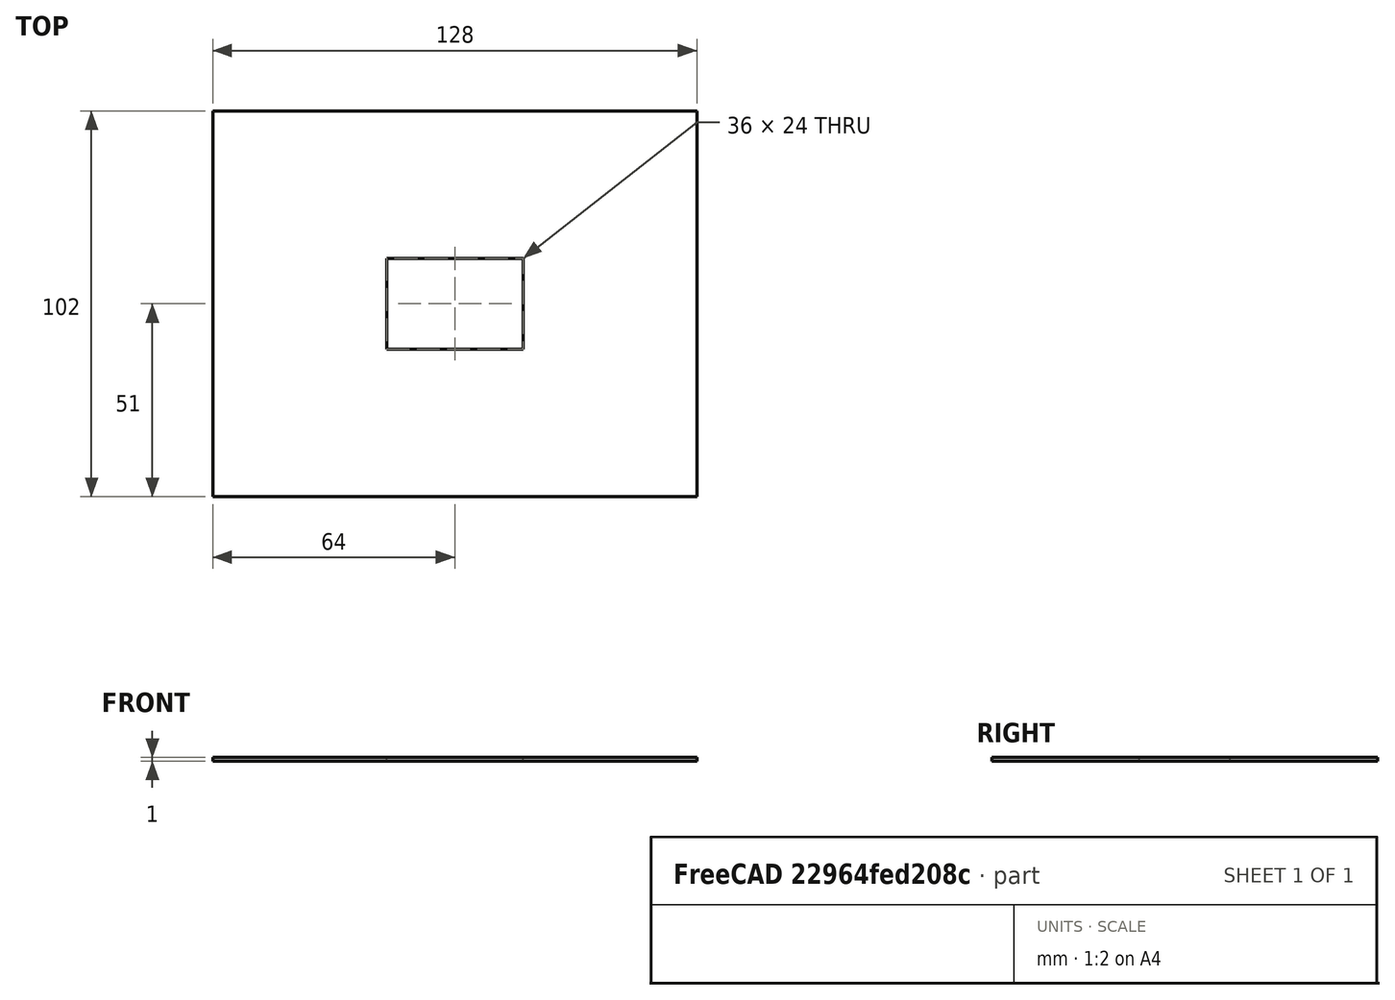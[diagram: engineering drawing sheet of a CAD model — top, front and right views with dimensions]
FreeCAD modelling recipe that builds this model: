
FCSTD DOCUMENT  (FreeCAD 0.18.4R)
Label: 35mm-mask
License: All rights reserved
LicenseURL: http://en.wikipedia.org/wiki/All_rights_reserved
objects: Sketcher::SketchObject×1, PartDesign::Pad×1, PartDesign::Body×1
note: 4 computed .brp shape members not serialized (recipe doc carries the construction recipe); baked Part::Feature solids carry a one-line shape summary decoded from their .brp

FEATURE [Sketcher::SketchObject] Sketch
  MapMode = 5
  Support = -> [XY_Plane]
  sketch-geometry (8):
    g0: LineSegment StartX=64 StartY=-51 StartZ=0 EndX=-64 EndY=-51 EndZ=0
    g1: LineSegment StartX=-64 StartY=-51 StartZ=0 EndX=-64 EndY=51 EndZ=0
    g2: LineSegment StartX=-64 StartY=51 StartZ=0 EndX=64 EndY=51 EndZ=0
    g3: LineSegment StartX=64 StartY=51 StartZ=0 EndX=64 EndY=-51 EndZ=0
    g4: LineSegment StartX=-18 StartY=12 StartZ=0 EndX=18 EndY=12 EndZ=0
    g5: LineSegment StartX=18 StartY=12 StartZ=0 EndX=18 EndY=-12 EndZ=0
    g6: LineSegment StartX=18 StartY=-12 StartZ=0 EndX=-18 EndY=-12 EndZ=0
    g7: LineSegment StartX=-18 StartY=-12 StartZ=0 EndX=-18 EndY=12 EndZ=0
  constraints (22):
    c: Coincident(g0,g1)
    c: Coincident(g1,g2)
    c: Coincident(g2,g3)
    c: Coincident(g3,g0)
    c: Horizontal(g0)
    c: Horizontal(g2)
    c: Vertical(g1)
    c: Vertical(g3)
    c: DistanceY(g3,g3) = 102
    c: DistanceX(g2,g2) = 128
    c: Coincident(g4,g5)
    c: Coincident(g5,g6)
    c: Coincident(g6,g7)
    c: Coincident(g7,g4)
    c: Horizontal(g4)
    c: Horizontal(g6)
    c: Vertical(g5)
    c: Vertical(g7)
    c: DistanceY(g5,g5) = 24
    c: DistanceX(g4,g4) = 36
    c: Symmetric(g2,g0,g-1)
    c: Symmetric(g5,g4,g-1)
FEATURE [PartDesign::Pad] Pad
  Length = 1
  Length2 = 117
  Profile = -> Sketch
  Type = 0
FEATURE [PartDesign::Body] Body
  Group = -> [Sketch,Pad]
  Origin = -> Origin
  Tip = -> Pad
